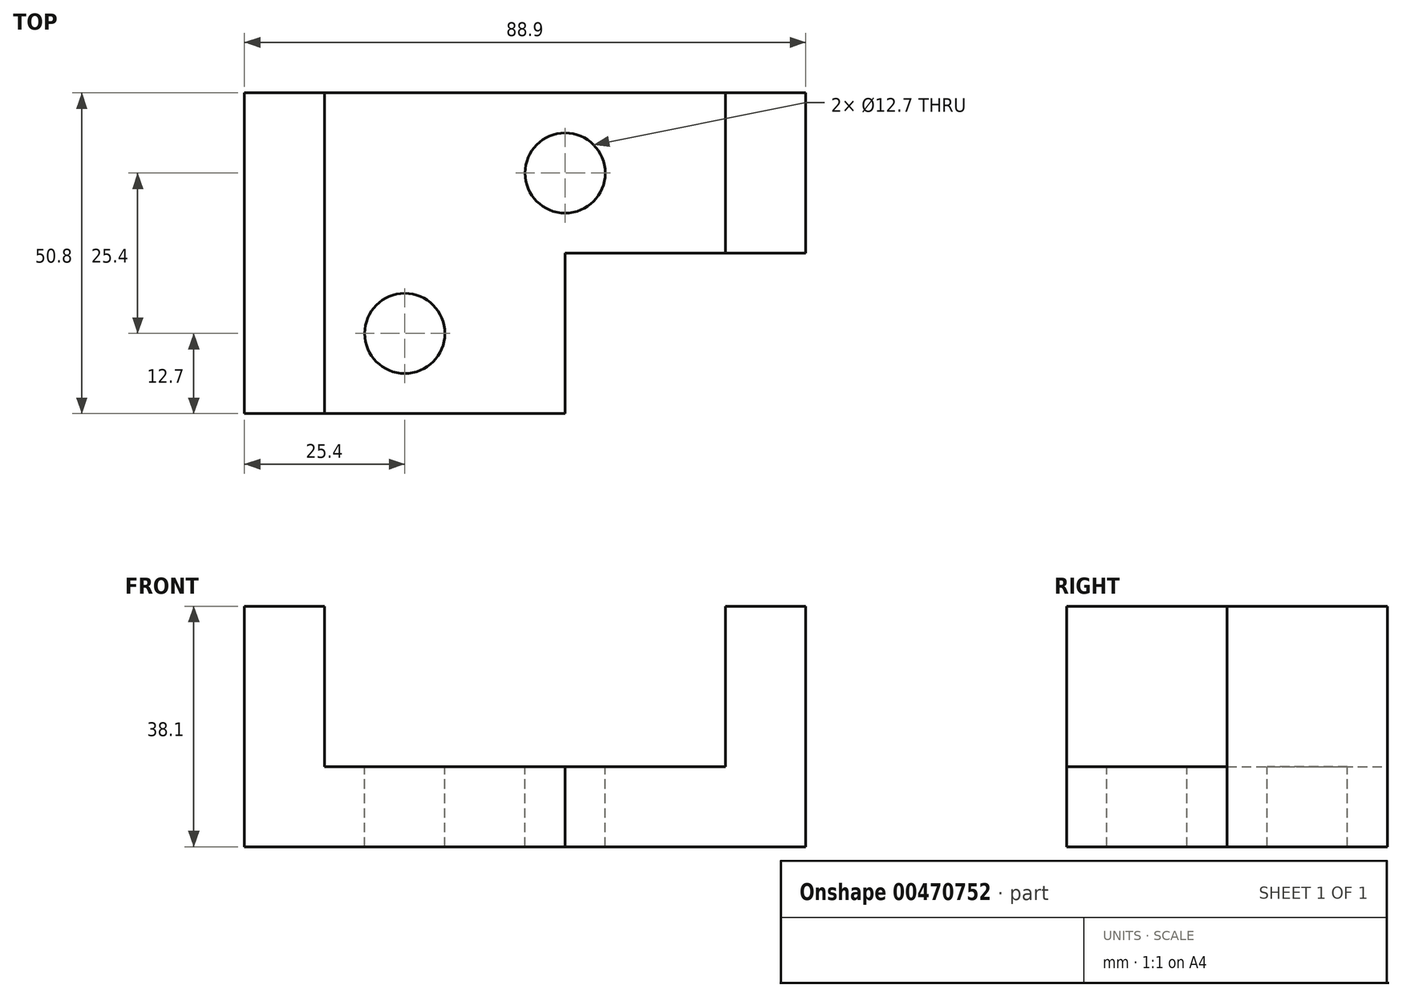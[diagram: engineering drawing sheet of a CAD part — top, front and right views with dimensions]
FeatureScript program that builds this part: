
annotation { "Feature Type Name" : "Feature", "Feature Type Description" : "" }
export const myFeature = defineFeature(function(context is Context, id is Id, definition is map)
    precondition{}
    {
        {
            var Q0;
            Q0=qCreatedBy(makeId("Front.planeOp"),FACE);
            var sketch = newSketch(context, id + "F0", { "sketchPlane" : qUnion([Q0])});
            skLineSegment(sketch, "E0.bottom", {"start": v(-44.45, 19.05) * mm, "end": v(44.45, 19.05) * mm});
            skLineSegment(sketch, "E0.top", {"start": v(-44.45, -19.05) * mm, "end": v(44.45, -19.05) * mm});
            skLineSegment(sketch, "E0.left", {"start": v(-44.45, 19.05) * mm, "end": v(-44.45, -19.05) * mm});
            skLineSegment(sketch, "E0.right", {"start": v(44.45, 19.05) * mm, "end": v(44.45, -19.05) * mm});
            skPoint(sketch, "E0.middle", {"position": v(0, 0) * mm});
            skLineSegment(sketch, "E1.bottom", {"start": v(-31.75, 19.05) * mm, "end": v(31.75, 19.05) * mm});
            skLineSegment(sketch, "E1.top", {"start": v(-31.75, -6.35) * mm, "end": v(31.75, -6.35) * mm});
            skLineSegment(sketch, "E1.left", {"start": v(-31.75, 19.05) * mm, "end": v(-31.75, -6.35) * mm});
            skLineSegment(sketch, "E1.right", {"start": v(31.75, 19.05) * mm, "end": v(31.75, -6.35) * mm});
            skSolve(sketch);
        }
        {
            var Q0;
            Q0=makeQuery(id+"F0.imprint","IMPRINT",FACE,{"disambiguationData":[TD([[makeQuery(id+"F0.imprint","IMPRINT",EDGE,{"derivedFrom":sQuery(id+"F0.wireOp",EDGE,"E0.top")}),1.0]])]});
            extrude(context, id + "F1", {"entities" : qUnion([Q0]), "depth" : 50.8 * mm});
        }
        {
            var Q0;
            Q0=makeQuery(id+"F1.opExtrude","SWEPT_FACE",FACE,{"disambiguationData":[OSD([sQuery(id+"F0.wireOp",EDGE,"E1.top")])]});
            var sketch = newSketch(context, id + "F2", { "sketchPlane" : qUnion([Q0])});
            skLineSegment(sketch, "E2.bottom", {"start": v(44.45, -50.8) * mm, "end": v(6.35, -50.8) * mm});
            skLineSegment(sketch, "E2.top", {"start": v(44.45, -25.4) * mm, "end": v(6.35, -25.4) * mm});
            skLineSegment(sketch, "E2.left", {"start": v(44.45, -50.8) * mm, "end": v(44.45, -25.4) * mm});
            skLineSegment(sketch, "E2.right", {"start": v(6.35, -50.8) * mm, "end": v(6.35, -25.4) * mm});
            skSolve(sketch);
        }
        {
            var Q0;
            {var subQ4=sQuery(id+"F2.wireOp",EDGE,"E2.right");Q0=makeQuery(id+"F2.imprint","IMPRINT",FACE,{"disambiguationData":[TD([[makeQuery(id+"F2.imprint","IMPRINT",EDGE,{"derivedFrom":subQ4}),-1.0]])]});}
            extrude(context, id + "F3", {"entities" : qUnion([Q0]), "operationType" : NewBodyOperationType.REMOVE, "endBound" : BoundingType.THROUGH_ALL, "oppositeDirection" : true, "depth" : 25.4 * mm});
        }
        {
            var Q0;
            {var subQ0=sQuery(id+"F0.wireOp",EDGE,"E0.bottom");Q0=makeQuery(id+"F1.opExtrude","SWEPT_FACE",FACE,{"disambiguationData":[OSD([subQ0]),TDD([makeQuery(id+"F0.imprint","IMPRINT",EDGE,{"disambiguationData":[TD([[makeQuery(id+"F0.imprint","INTERSECT",VERTEX,{"derivedFrom":[subQ0,sQuery(id+"F0.wireOp",EDGE,"E0.right")]}),1.0]])],"derivedFrom":subQ0})])]});}
            var sketch = newSketch(context, id + "F4", { "sketchPlane" : qUnion([Q0])});
            skLineSegment(sketch, "E3.bottom", {"start": v(31.75, -25.4) * mm, "end": v(44.45, -25.4) * mm});
            skLineSegment(sketch, "E3.top", {"start": v(31.75, -50.8) * mm, "end": v(44.45, -50.8) * mm});
            skLineSegment(sketch, "E3.left", {"start": v(31.75, -25.4) * mm, "end": v(31.75, -50.8) * mm});
            skLineSegment(sketch, "E3.right", {"start": v(44.45, -25.4) * mm, "end": v(44.45, -50.8) * mm});
            skSolve(sketch);
        }
        {
            var Q0;
            Q0=makeQuery(id+"F4.imprint","IMPRINT",FACE,{"disambiguationData":[TD([[makeQuery(id+"F4.imprint","IMPRINT",EDGE,{"derivedFrom":sQuery(id+"F4.wireOp",EDGE,"E3.bottom")}),-1.0]])]});
            extrude(context, id + "F5", {"entities" : qUnion([Q0]), "operationType" : NewBodyOperationType.REMOVE, "endBound" : BoundingType.THROUGH_ALL, "oppositeDirection" : true, "depth" : 25.4 * mm});
        }
        {
            var Q0;
            Q0=makeQuery(id+"F1.opExtrude","SWEPT_FACE",FACE,{"disambiguationData":[OSD([sQuery(id+"F0.wireOp",EDGE,"E1.top")])]});
            var sketch = newSketch(context, id + "F6", { "sketchPlane" : qUnion([Q0])});
            skCircle(sketch, "E4", {"center": v(6.35, -12.7) * mm, "radius": 6.35 * mm});
            skSolve(sketch);
        }
        {
            var Q0;
            Q0=makeQuery(id+"F6.imprint","IMPRINT",FACE,{"disambiguationData":[TD([[makeQuery(id+"F6.imprint","IMPRINT",EDGE,{"derivedFrom":sQuery(id+"F6.wireOp",EDGE,"E4")}),1.0]])]});
            extrude(context, id + "F7", {"entities" : qUnion([Q0]), "operationType" : NewBodyOperationType.REMOVE, "endBound" : BoundingType.THROUGH_ALL, "oppositeDirection" : true, "depth" : 25.4 * mm});
        }
        {
            var Q0;
            Q0=makeQuery(id+"F1.opExtrude","SWEPT_FACE",FACE,{"disambiguationData":[OSD([sQuery(id+"F0.wireOp",EDGE,"E1.top")])]});
            var sketch = newSketch(context, id + "F8", { "sketchPlane" : qUnion([Q0])});
            skCircle(sketch, "E5", {"center": v(-19.05, -38.1) * mm, "radius": 6.35 * mm});
            skSolve(sketch);
        }
        {
            var Q0;
            Q0=makeQuery(id+"F8.imprint","IMPRINT",FACE,{"disambiguationData":[TD([[makeQuery(id+"F8.imprint","IMPRINT",EDGE,{"derivedFrom":sQuery(id+"F8.wireOp",EDGE,"E5")}),1.0]])]});
            extrude(context, id + "F9", {"entities" : qUnion([Q0]), "operationType" : NewBodyOperationType.REMOVE, "endBound" : BoundingType.THROUGH_ALL, "oppositeDirection" : true, "depth" : 25.4 * mm});
        }
    });
